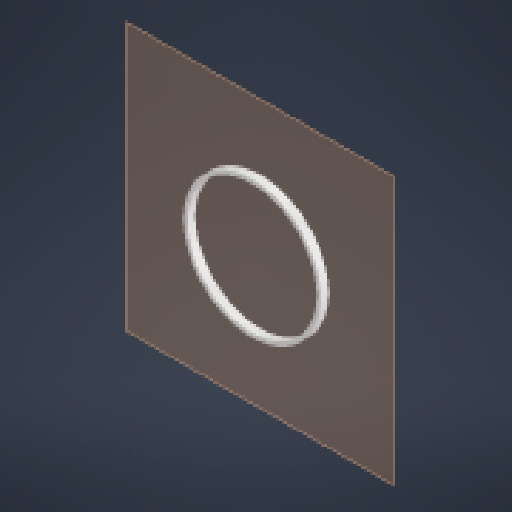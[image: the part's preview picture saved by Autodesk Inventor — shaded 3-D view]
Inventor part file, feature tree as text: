
AUTODESK INVENTOR PART (.ipt)
format: ipt  version: 2023.1 (Build 271208000, 208)  size: 178,176 bytes
history: native  units: mm
features: other x3, plane x1, extrude x1, sketch x1
ambient origin geometry x8: Origin, YZ Plane, XZ Plane, XY Plane, X Axis, Y Axis, Z Axis, Center Point
bodies: Solid1 (feature_tree)
feature tree (6):
  plane  "Work Plane1"
  extrude  "Extrusion1"  Depth=10.0mm
  sketch  "Sketch1"  dims[d0=157.0mm d1=5.0mm d2=10.0mm d3=0.0mm]
  parser-record x1  (decoder bookkeeping rows leaked as tree rows — omitted from the tree; the rows remain in map.json)
  other  "Beau4tClock.iam"
  other  "Clock:1"
note: 1 file-system path scrubbed to <path> (originals preserved in map.json)
